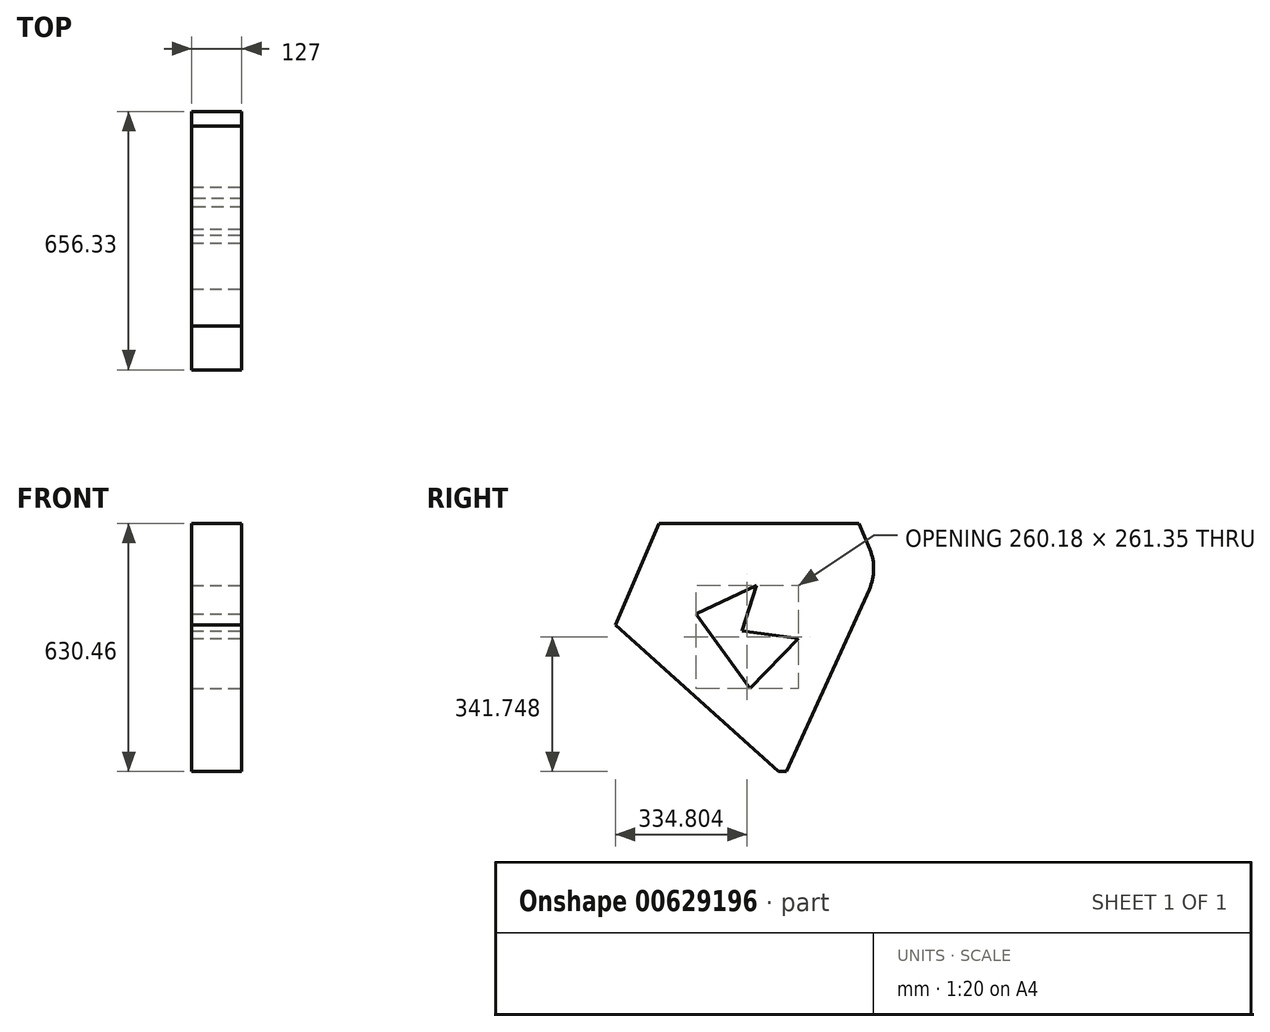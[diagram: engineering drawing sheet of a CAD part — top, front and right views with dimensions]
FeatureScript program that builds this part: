
annotation { "Feature Type Name" : "Feature", "Feature Type Description" : "" }
export const myFeature = defineFeature(function(context is Context, id is Id, definition is map)
    precondition{}
    {
        {
            var Q0;
            Q0=qCreatedBy(makeId("Right.planeOp"),FACE);
            var sketch = newSketch(context, id + "F0", { "sketchPlane" : qUnion([Q0])});
            skLineSegment(sketch, "E0", {"start": v(0, 0) * mm, "end": v(209.86, 462.94) * mm});
            skLineSegment(sketch, "E1", {"start": v(211.45, 564.16) * mm, "end": v(183.87, 630.46) * mm});
            skLineSegment(sketch, "E2", {"start": v(183.87, 630.46) * mm, "end": v(-324.13, 630.46) * mm});
            skLineSegment(sketch, "E3", {"start": v(-324.13, 630.46) * mm, "end": v(-435.13, 372.19) * mm});
            skLineSegment(sketch, "E4", {"start": v(-435.13, 372.19) * mm, "end": v(-21.34, 0) * mm});
            skLineSegment(sketch, "E5", {"start": v(-21.34, 0) * mm, "end": v(0, 0) * mm});
            skPoint(sketch, "E6.visualSharp", {"position": v(232.65, 513.2) * mm});
            skArc(sketch, "E6.filletArc", {"start": v(209.86, 462.94) * mm, "mid": v(221.18, 513.38) * mm, "end": v(211.45, 564.16) * mm});
            skSolve(sketch);
        }
        {
            var Q0;
            Q0=makeQuery(id+"F0.imprint","IMPRINT",FACE,{"disambiguationData":[TD([[makeQuery(id+"F0.imprint","IMPRINT",EDGE,{"derivedFrom":sQuery(id+"F0.wireOp",EDGE,"E0")}),1.0]])]});
            extrude(context, id + "F1", {"entities" : qUnion([Q0]), "depth" : 127 * mm, "offsetDistance" : 25.4 * mm});
        }
        {
            var Q0;
            Q0=makeQuery(id+"F1.opExtrude","CAP_FACE",FACE,{"disambiguationData":[OSD([sQuery(id+"F0.wireOp",EDGE,"E0"),sQuery(id+"F0.wireOp",EDGE,"E1"),sQuery(id+"F0.wireOp",EDGE,"E2"),sQuery(id+"F0.wireOp",EDGE,"E3"),sQuery(id+"F0.wireOp",EDGE,"E4"),sQuery(id+"F0.wireOp",EDGE,"E5"),sQuery(id+"F0.wireOp",EDGE,"E6.filletArc")])],"isStart":false});
            var sketch = newSketch(context, id + "F2", { "sketchPlane" : qUnion([Q0])});
            skLineSegment(sketch, "E7", {"start": v(-230.42, 400.57) * mm, "end": v(-92.96, 211.07) * mm});
            skLineSegment(sketch, "E8", {"start": v(-92.96, 211.07) * mm, "end": v(29.76, 337.93) * mm});
            skLineSegment(sketch, "E9", {"start": v(29.76, 337.93) * mm, "end": v(-113.03, 357.66) * mm});
            skLineSegment(sketch, "E10", {"start": v(-113.03, 357.66) * mm, "end": v(-77, 472.42) * mm});
            skLineSegment(sketch, "E11", {"start": v(-77, 472.42) * mm, "end": v(-230.42, 400.57) * mm});
            skSolve(sketch);
        }
        {
            var Q0;
            Q0=makeQuery(id+"F2.imprint","IMPRINT",FACE,{"disambiguationData":[TD([[makeQuery(id+"F2.imprint","IMPRINT",EDGE,{"derivedFrom":sQuery(id+"F2.wireOp",EDGE,"E7")}),1.0]])]});
            extrude(context, id + "F3", {"entities" : qUnion([Q0]), "operationType" : NewBodyOperationType.REMOVE, "oppositeDirection" : true, "depth" : 254 * mm, "offsetDistance" : 25.4 * mm});
        }
    });
